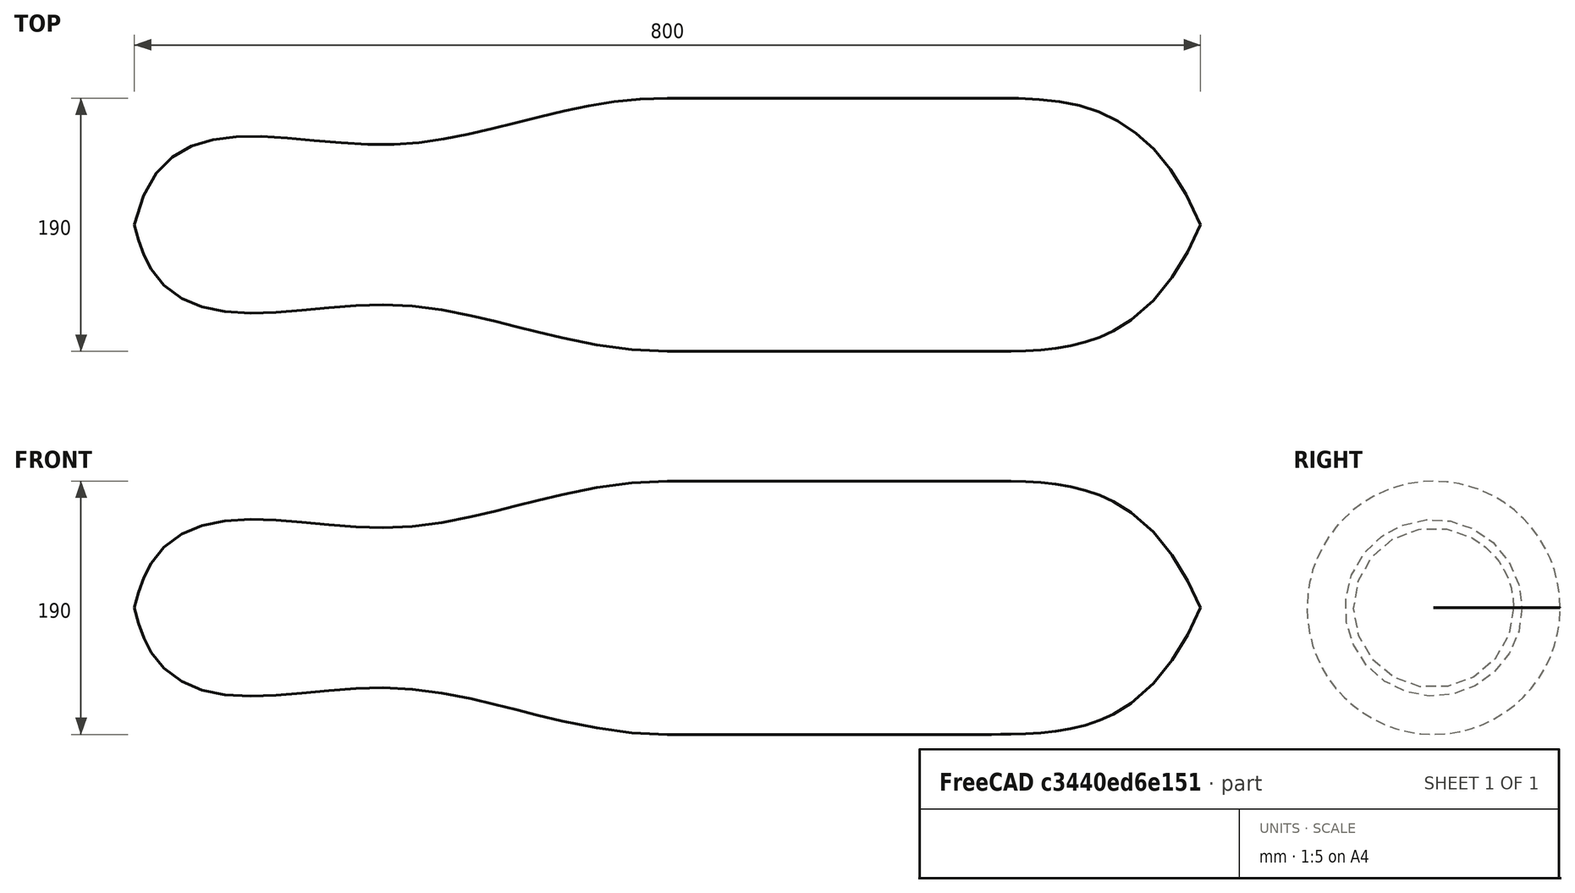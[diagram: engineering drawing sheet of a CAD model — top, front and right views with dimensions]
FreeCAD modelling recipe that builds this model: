
FCSTD DOCUMENT  (FreeCAD 0.19R24267 +99 (Git))
Label: free_hull
License: All rights reserved
LicenseURL: http://en.wikipedia.org/wiki/All_rights_reserved
objects: Sketcher::SketchObject×1, PartDesign::Revolution×1, PartDesign::Body×1, TechDraw::DrawSVGTemplate×1, TechDraw::DrawViewPart×1, TechDraw::DrawViewSection×1, TechDraw::DrawPage×1
note: 4 computed .brp shape members not serialized (recipe doc carries the construction recipe); baked Part::Feature solids carry a one-line shape summary decoded from their .brp

FEATURE [Sketcher::SketchObject] Sketch
  FullyConstrained = true
  MapMode = 5
  Support = -> [XY_Plane]
  expr: Constraints[43] = .Constraints.part_a * 0.05
  expr: Constraints[44] = .Constraints.part_a * 0.5
  expr: Constraints[48] = .Constraints.part_b * 0.9
  expr: Constraints[45] = .Constraints.part_a * 0.8
  expr: Constraints[46] = .Constraints.part_b * 0.3
  expr: Constraints[47] = .Constraints.part_b * 0.6
  sketch-geometry (19):
    g0: LineSegment StartX=-200 StartY=95 StartZ=0 EndX=-200 EndY=0 EndZ=0
    g1: LineSegment StartX=-200 StartY=0 StartZ=0 EndX=200 EndY=-2e-16 EndZ=0
    g2: LineSegment StartX=-200 StartY=0 StartZ=0 EndX=-600 EndY=0 EndZ=0
    g3-g7: Circle x5 (B-spline internal-alignment scaffolding for g8; pole/knot coordinates omitted)
    g8: BSplineCurve PolesCount=5 KnotsCount=3 Degree=3 IsPeriodic=0
    g9: GeomPoint X=-600 Y=0 Z=0
    g10: GeomPoint X=-200 Y=95 Z=0
    g11-g15: Circle x5 (B-spline internal-alignment scaffolding for g16; pole/knot coordinates omitted)
    g16: BSplineCurve PolesCount=5 KnotsCount=3 Degree=3 IsPeriodic=0
    g17: GeomPoint X=-200 Y=95 Z=0
    g18: GeomPoint X=200 Y=-2e-16 Z=0
  constraints (35):
    c: Vertical(g0)
    c: Symmetric(g0,g1,g-2)
    c: Coincident(g1,g0)
    c: Coincident(g2,g0)
    c: PointOnObject(g2,g-1)
    c: Horizontal(g2)
    c: Coincident(g8,g2)
    c: Weight(g3) = 1
    c: Equal(g3, g4-g7) x4
    c: Coincident(g8,g0)
    c: InternalAlignment(g3-g7 -> g8) x5
    c: InternalAlignment(g9,g8)
    c: InternalAlignment(g10,g8)
    c: Coincident(g16,g8)
    c: Weight(g11) = 1
    c: Equal(g11, g12-g15) x4
    c: Coincident(g16,g1)
    c: InternalAlignment(g11-g15 -> g16) x5
    c: InternalAlignment(g17,g16)
    c: InternalAlignment(g18,g16)
    c: DistanceX(g2,g1) = 400  'part_a'
    c: DistanceX(g1,g1) = 400  'part_b'
    c: DistanceY(g1,g8) = 95  'radius'
    c: DistanceY(g2,g4) = 95  'first_y'
    c: DistanceY(g2,g5) = 25  'second_y'
    c: DistanceY(g2,g6) = 95  'third_y'
    c: DistanceY(g2,g12) = 95  'fourth_y'
    c: DistanceY(g2,g13) = 95  'fifth_y'
    c: DistanceY(g2,g14) = 95  'sixth_y'
    c: DistanceX(g2,g4) = 20
    c: DistanceX(g2,g5) = 200
    c: DistanceX(g2,g6) = 320
    c: DistanceX(g1,g12) = 120
    c: DistanceX(g1,g13) = 240
    c: DistanceX(g1,g14) = 360
FEATURE [PartDesign::Revolution] Revolution
  Angle = 360
  Axis = (1,0,0)
  Base = (0,0,0)
  Profile = -> Sketch
  ReferenceAxis = -> Sketch [H_Axis]
FEATURE [PartDesign::Body] Body
  Group = -> [Sketch,Revolution]
  Origin = -> Origin
  Tip = -> Revolution
FEATURE [TechDraw::DrawSVGTemplate] Template
  EditableTexts = Designed_by_Name=Designed by Name; Drawing_number=Drawing number; FC-Date=Date; FC-SC=Scale; FC-SH=Sheet; FC-Title=Title; Subtitle=Subtitle; Weight=Weight
  Height = 210
  Orientation = 1
  Width = 297
FEATURE [TechDraw::DrawViewPart] View
  CoarseView = false
  Direction = (0,0,1)
  Focus = 100
  HardHidden = false
  IsoCount = 0
  IsoHidden = false
  IsoVisible = false
  LockPosition = false
  Perspective = false
  Rotation = 0
  Scale = 0.05
  ScaleType = 0
  SeamHidden = false
  SeamVisible = true
  SmoothHidden = false
  SmoothVisible = true
  Source = -> [Body]
  X = 65.7614
  XDirection = (1,0,0)
  Y = 42.7117
FEATURE [TechDraw::DrawViewSection] SectionView  label="Section  - "
  BaseView = -> View
  CoarseView = false
  CutSurfaceDisplay = 2
  Direction = (0,1,0)
  FileGeomPattern = <path>
  FileHatchPattern = <path>
  Focus = 100
  FuseBeforeCut = false
  HardHidden = false
  HatchScale = 1
  IsoCount = 0
  IsoHidden = false
  IsoVisible = false
  LockPosition = false
  NameGeomPattern = Diamond
  Perspective = false
  Rotation = 0
  Scale = 0.1
  ScaleType = 0
  SeamHidden = false
  SeamVisible = true
  SectionDirection = 3
  SectionNormal = (0,1,0)
  SectionOrigin = (0,0,0)
  SmoothHidden = false
  SmoothVisible = true
  Source = -> [Body]
  X = 144.754
  XDirection = (1,0,0)
  Y = 127.102
FEATURE [TechDraw::DrawPage] Page
  KeepUpdated = true
  NextBalloonIndex = 1
  ProjectionType = 0
  Template = -> Template
  Views = -> [View,SectionView]
note: 2 file-system paths scrubbed to <path> (originals preserved in the JSON sidecar)
